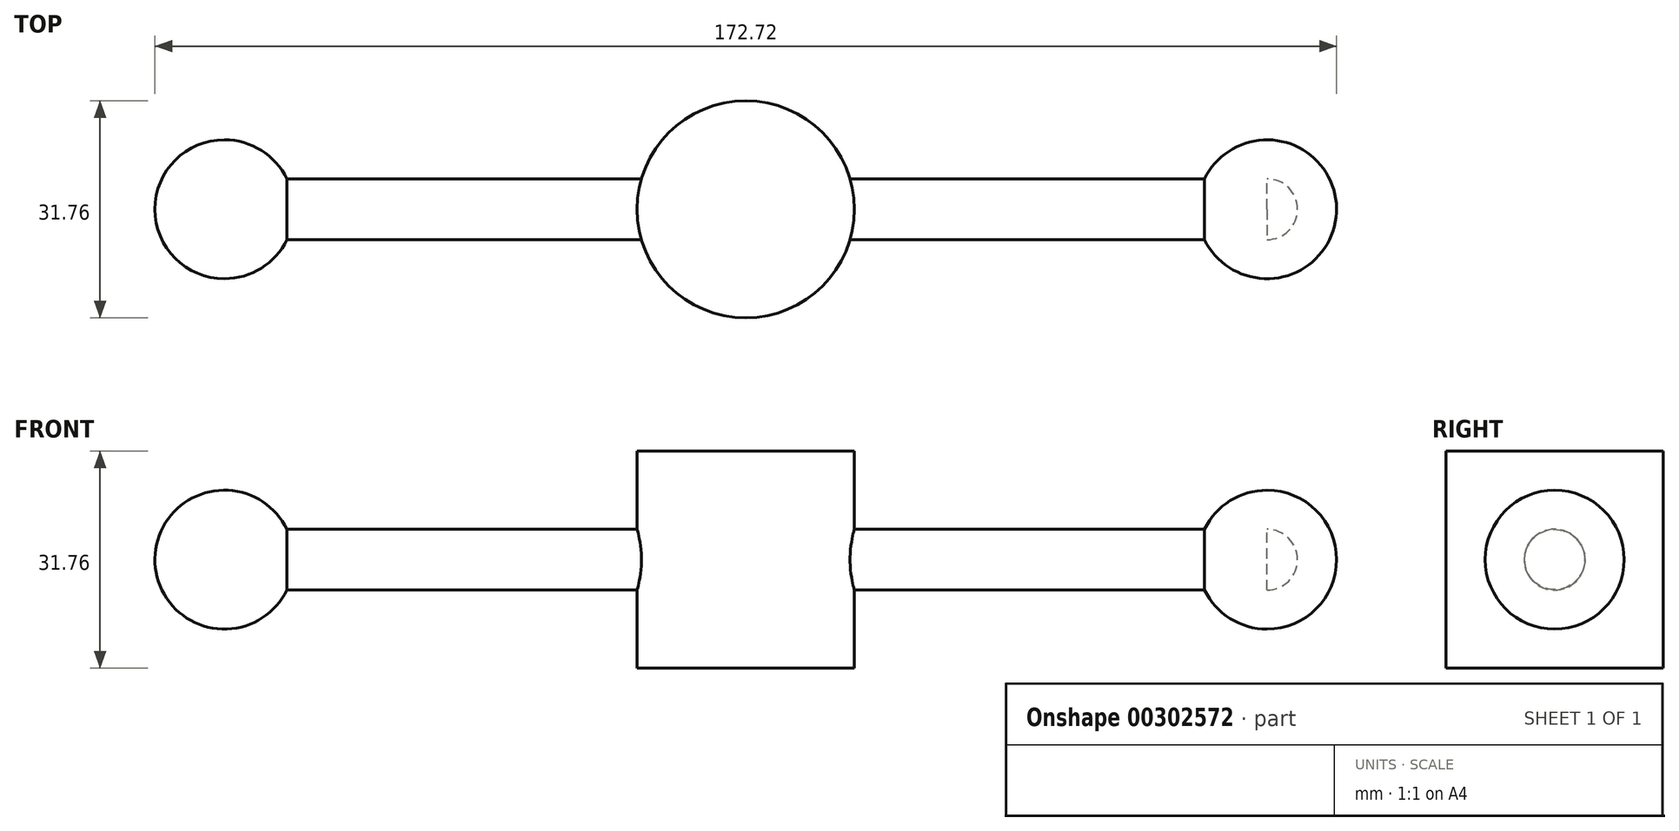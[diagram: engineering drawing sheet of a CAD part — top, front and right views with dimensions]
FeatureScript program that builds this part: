
annotation { "Feature Type Name" : "Feature", "Feature Type Description" : "" }
export const myFeature = defineFeature(function(context is Context, id is Id, definition is map)
    precondition{}
    {
        {
            var Q0;
            Q0=qCreatedBy(makeId("Top.planeOp"),FACE);
            var sketch = newSketch(context, id + "F0", { "sketchPlane" : qUnion([Q0])});
            skCircle(sketch, "E0", {"center": v(0, 0) * mm, "radius": 15.88 * mm});
            skCircle(sketch, "E1", {"center": v(0, 0) * mm, "radius": 6.35 * mm});
            skSolve(sketch);
        }
        {
            var Q0;
            Q0=makeQuery(id+"F0.imprint","IMPRINT",FACE,{"disambiguationData":[TD([[makeQuery(id+"F0.imprint","IMPRINT",EDGE,{"derivedFrom":sQuery(id+"F0.wireOp",EDGE,"E0")}),1.0]])]});
            var Q1;
            Q1=makeQuery(id+"F0.imprint","IMPRINT",FACE,{"disambiguationData":[TD([[makeQuery(id+"F0.imprint","IMPRINT",EDGE,{"derivedFrom":sQuery(id+"F0.wireOp",EDGE,"E1")}),1.0]])]});
            extrude(context, id + "F1", {"entities" : qUnion([Q0, Q1]), "endBound" : BoundingType.SYMMETRIC, "depth" : 31.75 * mm});
        }
        {
            var Q0;
            Q0=makeQuery(id+"F0.imprint","IMPRINT",FACE,{"disambiguationData":[TD([[makeQuery(id+"F0.imprint","IMPRINT",EDGE,{"derivedFrom":sQuery(id+"F0.wireOp",EDGE,"E1")}),1.0]])]});
            var Q1;
            Q1=sQuery(id+"F0.wireOp",EDGE,"E1");
            extrude(context, id + "F2", {"entities" : qUnion([Q0]), "operationType" : NewBodyOperationType.ADD, "surfaceEntities" : qUnion([Q1]), "oppositeDirection" : true, "depth" : ((1.25 / 2) + (3 - 1.25)) * mm});
        }
        {
            var Q0;
            Q0=qCreatedBy(makeId("Right.planeOp"),FACE);
            var sketch = newSketch(context, id + "F3", { "sketchPlane" : qUnion([Q0])});
            skCircle(sketch, "E2", {"center": v(0, 0) * mm, "radius": 4.45 * mm});
            skSolve(sketch);
        }
        {
            var Q0;
            Q0=makeQuery(id+"F3.imprint","IMPRINT",FACE,{"disambiguationData":[TD([[makeQuery(id+"F3.imprint","IMPRINT",EDGE,{"derivedFrom":sQuery(id+"F3.wireOp",EDGE,"E2")}),1.0]])]});
            var Q1;
            Q1=sQuery(id+"F3.wireOp",EDGE,"E2");
            extrude(context, id + "F4", {"entities" : qUnion([Q0]), "operationType" : NewBodyOperationType.ADD, "surfaceEntities" : qUnion([Q1]), "endBound" : BoundingType.SYMMETRIC, "depth" : 152.4 * mm});
        }
        {
            var Q0;
            Q0=makeQuery(id+"F4.opExtrude","CAP_FACE",FACE,{"disambiguationData":[OSD([sQuery(id+"F3.wireOp",EDGE,"E2")])],"isStart":false});
            var sketch = newSketch(context, id + "F5", { "sketchPlane" : qUnion([Q0])});
            skLineSegment(sketch, "E3", {"start": v(0, 4.45) * mm, "end": v(0, -4.45) * mm});
            skCircle(sketch, "E4", {"center": v(0, 0) * mm, "radius": 10.16 * mm});
            skLineSegment(sketch, "E5", {"start": v(0, 10.16) * mm, "end": v(0, -10.16) * mm});
            skSolve(sketch);
        }
        {
            var Q0;
            {var subQ0=sQuery(id+"F5.wireOp",EDGE,"E5");var subQ1=sQuery(id+"F5.wireOp",EDGE,"E4");var subQ2=makeQuery(id+"F5.imprint","INTERSECT",VERTEX,{"disambiguationData":[OD(0.0)],"derivedFrom":[subQ1,subQ0]});Q0=makeQuery(id+"F5.imprint","IMPRINT",FACE,{"disambiguationData":[TD([[makeQuery(id+"F5.imprint","IMPRINT",EDGE,{"disambiguationData":[TD([[subQ2,1.0]])],"derivedFrom":subQ1}),1.0]])]});}
            var Q1;
            {var subQ0=sQuery(id+"F5.wireOp",EDGE,"E5");var subQ1=makeQuery(id+"F4.opExtrude","CAP_EDGE",EDGE,{"disambiguationData":[OSD([sQuery(id+"F3.wireOp",EDGE,"E2")])],"isStart":false});var subQ2=makeQuery(id+"F5.imprint","INTERSECT",VERTEX,{"disambiguationData":[OD(0.0)],"derivedFrom":[subQ1,subQ0]});Q1=makeQuery(id+"F5.imprint","IMPRINT",FACE,{"disambiguationData":[TD([[makeQuery(id+"F5.imprint","IMPRINT",EDGE,{"disambiguationData":[TD([[subQ2,-1.0]])],"derivedFrom":subQ0}),1.0]])]});}
            var Q2;
            Q2=sQuery(id+"F5.wireOp",EDGE,"E5");
            revolve(context, id + "F6", {"operationType" : NewBodyOperationType.ADD, "entities" : qUnion([Q0, Q1]), "axis" : qUnion([Q2]), "revolveType" : RevolveType.FULL});
        }
        {
            var Q0;
            Q0=makeQuery(id+"F4.opExtrude","CAP_FACE",FACE,{"disambiguationData":[OSD([sQuery(id+"F3.wireOp",EDGE,"E2")])],"isStart":true});
            var sketch = newSketch(context, id + "F7", { "sketchPlane" : qUnion([Q0])});
            skCircle(sketch, "E6", {"center": v(0, 0) * mm, "radius": 10.16 * mm});
            skLineSegment(sketch, "E7", {"start": v(-11.88, 0) * mm, "end": v(11.48, 0) * mm, "construction": true});
            skLineSegment(sketch, "E8", {"start": v(-10.16, 0) * mm, "end": v(10.16, 0) * mm});
            skSolve(sketch);
        }
        {
            var Q0;
            {var subQ0=sQuery(id+"F7.wireOp",EDGE,"E8");var subQ1=sQuery(id+"F7.wireOp",EDGE,"E6");var subQ2=makeQuery(id+"F7.imprint","INTERSECT",VERTEX,{"disambiguationData":[OD(0.0)],"derivedFrom":[subQ1,subQ0]});Q0=makeQuery(id+"F7.imprint","IMPRINT",FACE,{"disambiguationData":[TD([[makeQuery(id+"F7.imprint","IMPRINT",EDGE,{"disambiguationData":[TD([[subQ2,1.0]])],"derivedFrom":subQ1}),1.0]])]});}
            var Q1;
            {var subQ0=sQuery(id+"F7.wireOp",EDGE,"E8");var subQ1=makeQuery(id+"F4.opExtrude","CAP_EDGE",EDGE,{"disambiguationData":[OSD([sQuery(id+"F3.wireOp",EDGE,"E2")])],"isStart":true});var subQ2=makeQuery(id+"F7.imprint","INTERSECT",VERTEX,{"disambiguationData":[OD(0.0)],"derivedFrom":[subQ1,subQ0]});Q1=makeQuery(id+"F7.imprint","IMPRINT",FACE,{"disambiguationData":[TD([[makeQuery(id+"F7.imprint","IMPRINT",EDGE,{"disambiguationData":[TD([[subQ2,-1.0]])],"derivedFrom":subQ0}),1.0]])]});}
            var Q2;
            Q2=sQuery(id+"F7.wireOp",EDGE,"E8");
            revolve(context, id + "F8", {"operationType" : NewBodyOperationType.ADD, "entities" : qUnion([Q0, Q1]), "axis" : qUnion([Q2]), "revolveType" : RevolveType.FULL});
        }
    });
